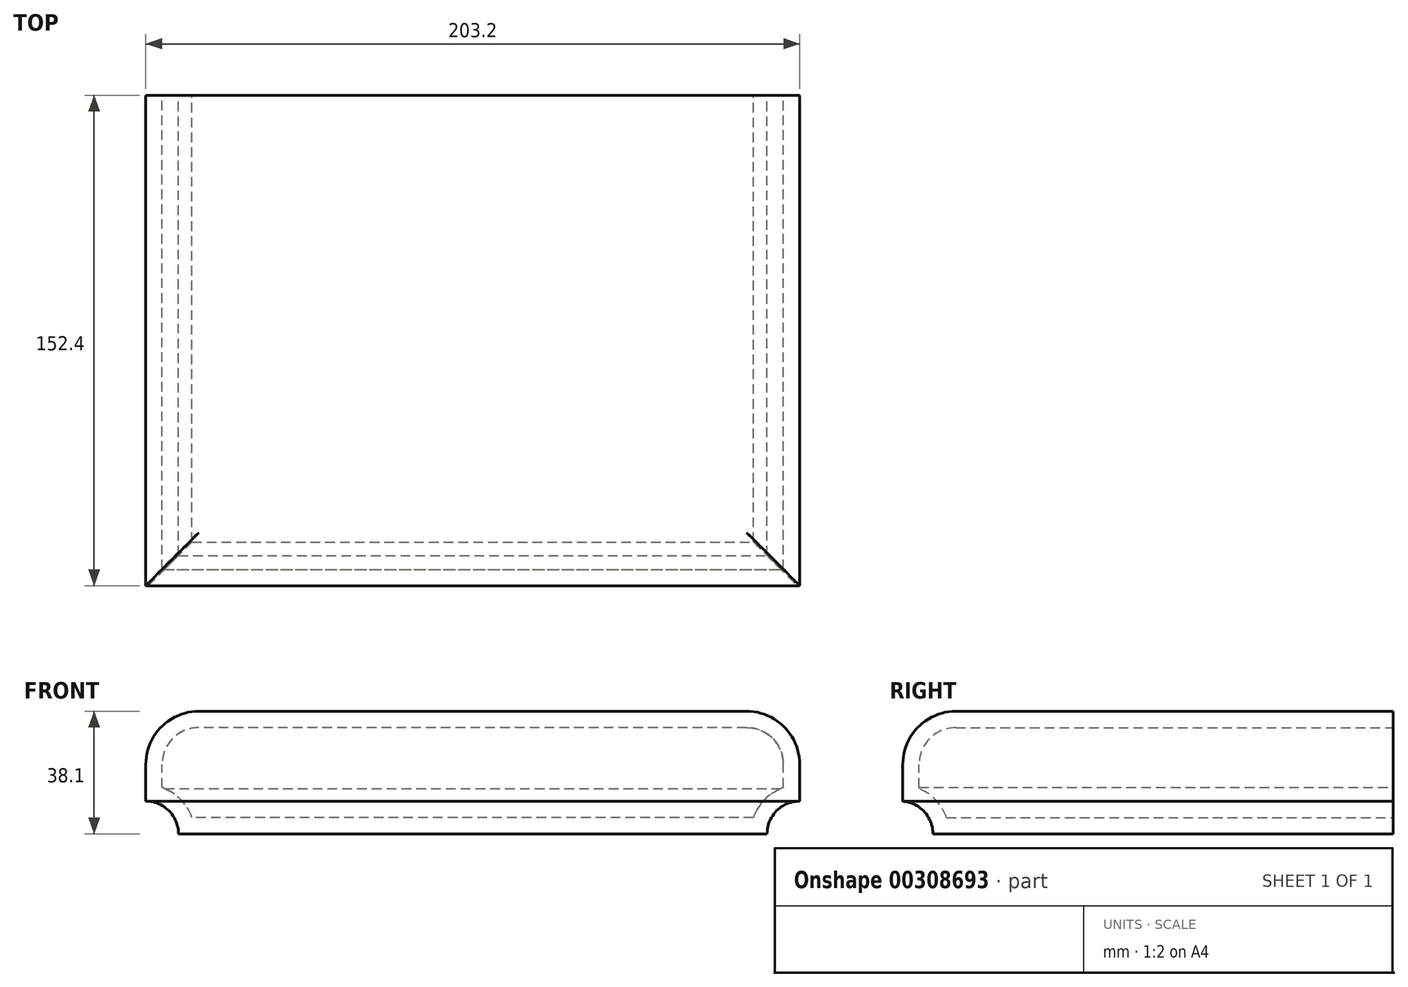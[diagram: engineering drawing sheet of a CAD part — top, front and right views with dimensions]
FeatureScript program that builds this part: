
annotation { "Feature Type Name" : "Feature", "Feature Type Description" : "" }
export const myFeature = defineFeature(function(context is Context, id is Id, definition is map)
    precondition{}
    {
        {
            var Q0;
            Q0=qCreatedBy(makeId("Front.planeOp"),FACE);
            var sketch = newSketch(context, id + "F0", { "sketchPlane" : qUnion([Q0])});
            skLineSegment(sketch, "E0.bottom", {"start": v(-10.16, 0) * mm, "end": v(-193.04, 0) * mm});
            skLineSegment(sketch, "E0.top", {"start": v(0, 38.1) * mm, "end": v(-203.2, 38.1) * mm});
            skLineSegment(sketch, "E0.left", {"start": v(0, 10.16) * mm, "end": v(0, 38.1) * mm});
            skLineSegment(sketch, "E0.right", {"start": v(-203.2, 10.16) * mm, "end": v(-203.2, 38.1) * mm});
            skArc(sketch, "E1", {"start": v(0, 10.16) * mm, "mid": v(-7.18, 7.18) * mm, "end": v(-10.16, 0) * mm});
            skArc(sketch, "E2", {"start": v(-193.04, 0) * mm, "mid": v(-196.02, 7.18) * mm, "end": v(-203.2, 10.16) * mm});
            skSolve(sketch);
        }
        {
            var Q0;
            Q0=makeQuery(id+"F0.imprint","IMPRINT",FACE,{"disambiguationData":[TD([[makeQuery(id+"F0.imprint","IMPRINT",EDGE,{"derivedFrom":sQuery(id+"F0.wireOp",EDGE,"E0.bottom")}),-1.0]])]});
            extrude(context, id + "F4", {"entities" : qUnion([Q0]), "depth" : 152.4 * mm});
        }
        {
            var Q0;
            Q0=makeQuery(id+"F4.opExtrude","SWEPT_FACE",FACE,{"disambiguationData":[OSD([sQuery(id+"F0.wireOp",EDGE,"E0.left")])]});
            var sketch = newSketch(context, id + "F1", { "sketchPlane" : qUnion([Q0])});
            skCircle(sketch, "E3", {"center": v(-153.18, 0) * mm, "radius": 10.16 * mm});
            skSolve(sketch);
        }
        {
            var Q0;
            Q0 = qSketchRegion(id + "F1", true);
            extrude(context, id + "F2", {"entities" : qUnion([Q0]), "operationType" : NewBodyOperationType.REMOVE, "oppositeDirection" : true, "depth" : 254 * mm});
        }
        {
            var Q0;
            Q0=makeQuery(id+"F4.opExtrude","CAP_EDGE",EDGE,{"disambiguationData":[OSD([sQuery(id+"F0.wireOp",EDGE,"E0.top")])],"isStart":false});
            var Q1;
            Q1=makeQuery(id+"F4.opExtrude","SWEPT_EDGE",EDGE,{"disambiguationData":[OSD([sQuery(id+"F0.wireOp",EDGE,"E0.top"),sQuery(id+"F0.wireOp",EDGE,"E0.right")])]});
            var Q2;
            Q2=makeQuery(id+"F4.opExtrude","SWEPT_EDGE",EDGE,{"disambiguationData":[OSD([sQuery(id+"F0.wireOp",EDGE,"E0.top"),sQuery(id+"F0.wireOp",EDGE,"E0.left")])]});
            fillet(context, id + "F3", {"entities" : qUnion([Q0, Q1, Q2]), "radius" : 16.5 * mm, "tangentPropagation" : true, "allowEdgeOverflow" : false});
        }
        {
            var Q0;
            Q0=makeQuery(id+"F4.opExtrude","CAP_FACE",FACE,{"disambiguationData":[OSD([sQuery(id+"F0.wireOp",EDGE,"E0.bottom"),sQuery(id+"F0.wireOp",EDGE,"E0.top"),sQuery(id+"F0.wireOp",EDGE,"E0.left"),sQuery(id+"F0.wireOp",EDGE,"E0.right"),sQuery(id+"F0.wireOp",EDGE,"E1"),sQuery(id+"F0.wireOp",EDGE,"E2")])],"isStart":true});
            shell(context, id + "F5", {"entities" : qUnion([Q0]), "thickness" : 5.08 * mm});
        }
    });
